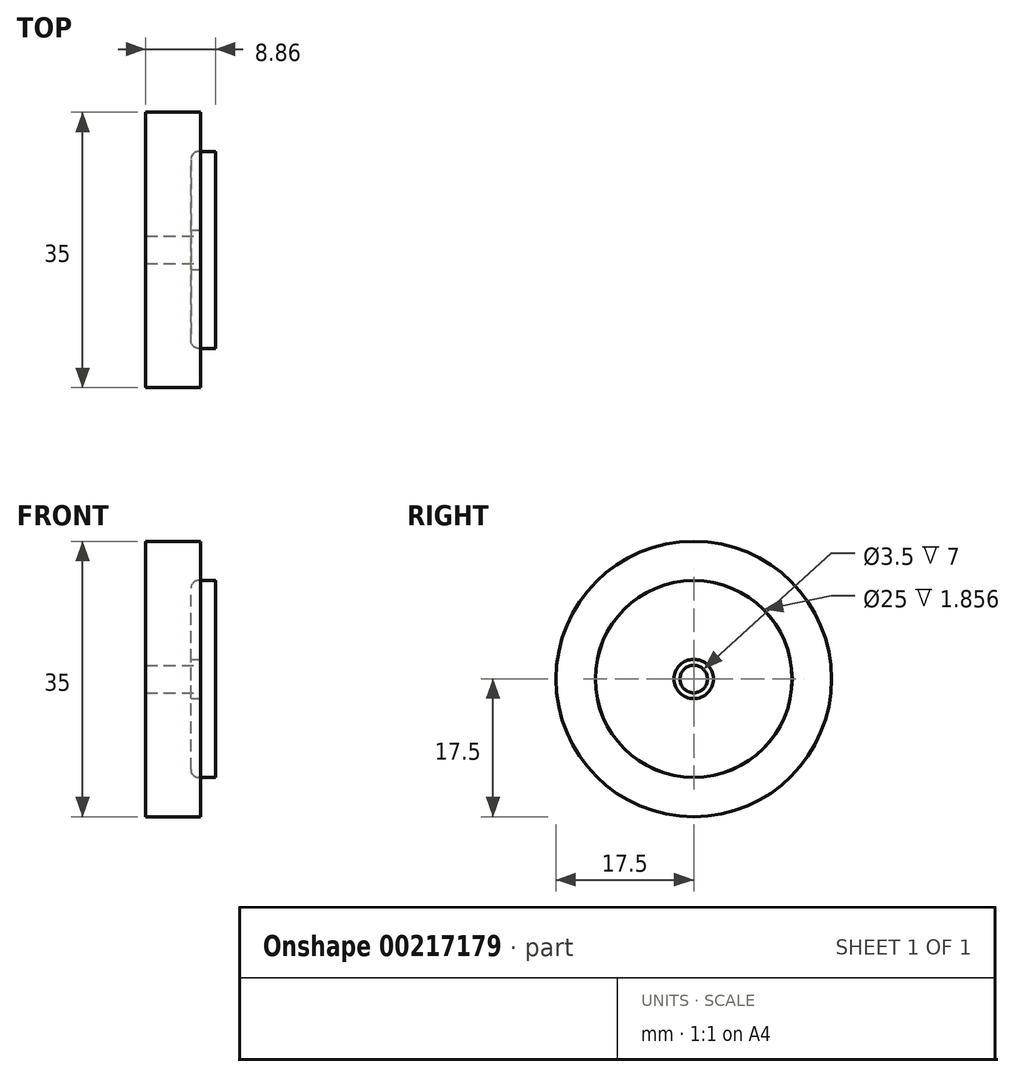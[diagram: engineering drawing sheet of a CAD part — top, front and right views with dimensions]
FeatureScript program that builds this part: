
annotation { "Feature Type Name" : "Feature", "Feature Type Description" : "" }
export const myFeature = defineFeature(function(context is Context, id is Id, definition is map)
    precondition{}
    {
        {
            var Q0;
            Q0=qCreatedBy(makeId("Front.planeOp"),FACE);
            var sketch = newSketch(context, id + "F0", { "sketchPlane" : qUnion([Q0])});
            skLineSegment(sketch, "E0", {"start": v(0, 0) * mm, "end": v(0, 17.5) * mm});
            skLineSegment(sketch, "E1", {"start": v(0, 17.5) * mm, "end": v(7, 17.5) * mm});
            skLineSegment(sketch, "E2", {"start": v(7, 17.5) * mm, "end": v(7, 12.5) * mm});
            skLineSegment(sketch, "E3", {"start": v(8.86, 12.5) * mm, "end": v(7, 12.5) * mm});
            skLineSegment(sketch, "E4", {"start": v(7, 2.5) * mm, "end": v(7, 0) * mm});
            skLineSegment(sketch, "E5", {"start": v(7, 0) * mm, "end": v(0, 0) * mm});
            skLineSegment(sketch, "E6", {"start": v(7, 2.5) * mm, "end": v(5.74, 2.5) * mm});
            skLineSegment(sketch, "E7", {"start": v(5.74, 2.5) * mm, "end": v(5.74, 11.5) * mm});
            skLineSegment(sketch, "E8", {"start": v(6.75, 12.5) * mm, "end": v(8.84, 12.5) * mm});
            skPoint(sketch, "E9.visualSharp", {"position": v(8.85, 12.5) * mm});
            skArc(sketch, "E9.filletArc", {"start": v(8.84, 12.5) * mm, "mid": v(8.85, 12.5) * mm, "end": v(8.86, 12.5) * mm});
            skPoint(sketch, "E10.visualSharp", {"position": v(5.74, 12.51) * mm});
            skArc(sketch, "E10.filletArc", {"start": v(6.75, 12.5) * mm, "mid": v(6.04, 12.22) * mm, "end": v(5.74, 11.5) * mm});
            skLineSegment(sketch, "E11", {"start": v(-74.93, 0) * mm, "end": v(75.1, 0) * mm, "construction": true});
            skSolve(sketch);
        }
        {
            var Q0;
            Q0 = qSketchRegion(id + "F0", true);
            var Q1;
            Q1=sQuery(id+"F0.wireOp",EDGE,"E5");
            revolve(context, id + "F1", {"entities" : qUnion([Q0]), "axis" : qUnion([Q1]), "revolveType" : RevolveType.FULL});
        }
        {
            var Q0;
            Q0=makeQuery(id+"F1.opRevolve","SWEPT_FACE",FACE,{"disambiguationData":[OSD([sQuery(id+"F0.wireOp",EDGE,"E4")])]});
            var sketch = newSketch(context, id + "F2", { "sketchPlane" : qUnion([Q0])});
            skCircle(sketch, "E12", {"center": v(0, 0) * mm, "radius": 1.75 * mm});
            skSolve(sketch);
        }
        {
            var Q0;
            Q0=makeQuery(id+"F2.imprint","IMPRINT",FACE,{"disambiguationData":[TD([[makeQuery(id+"F2.imprint","IMPRINT",EDGE,{"derivedFrom":sQuery(id+"F2.wireOp",EDGE,"E12")}),1.0]])]});
            extrude(context, id + "F3", {"entities" : qUnion([Q0]), "operationType" : NewBodyOperationType.REMOVE, "oppositeDirection" : true, "depth" : 25 * mm});
        }
    });
